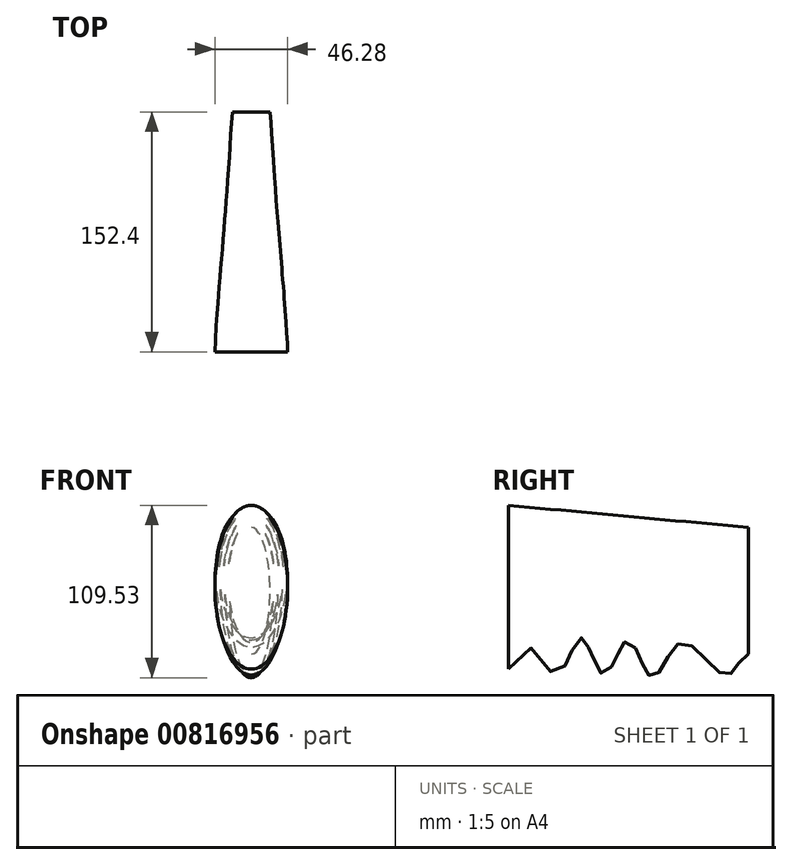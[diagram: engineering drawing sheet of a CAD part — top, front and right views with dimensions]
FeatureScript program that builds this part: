
annotation { "Feature Type Name" : "Feature", "Feature Type Description" : "" }
export const myFeature = defineFeature(function(context is Context, id is Id, definition is map)
    precondition{}
    {
        {
            var Q0;
            Q0=qCreatedBy(makeId("Front.planeOp"),FACE);
            var sketch = newSketch(context, id + "F0", { "sketchPlane" : qUnion([Q0])});
            skEllipse(sketch, "E0", {"center": v(0, -2.3) * mm, "majorRadius": 40.19 * mm, "minorRadius": 11.9 * mm, "majorAxis": v(0, 1)});
            skPoint(sketch, "E1", {"position": v(0, 37.89) * mm});
            skPoint(sketch, "E2", {"position": v(0, -42.49) * mm});
            skSolve(sketch);
        }
        {
            var Q0;
            Q0=qCreatedBy(makeId("Front.planeOp"),FACE);
            cPlane(context, id + "F1", {"entities" : qUnion([Q0]), "cplaneType" : CPlaneType.OFFSET, "offset" : 152.4 * mm, "width" : 152.4 * mm, "height" : 152.4 * mm});
        }
        {
            var Q0;
            Q0=qCreatedBy(id+"F1.planeOp",FACE);
            var sketch = newSketch(context, id + "F2", { "sketchPlane" : qUnion([Q0])});
            skEllipse(sketch, "E3", {"center": v(0, 0) * mm, "majorRadius": 52.02 * mm, "minorRadius": 23.14 * mm, "majorAxis": v(0, 1)});
            skPoint(sketch, "E4", {"position": v(0, 52.02) * mm});
            skPoint(sketch, "E5", {"position": v(0, -52.02) * mm});
            skSolve(sketch);
        }
        {
            var Q0;
            Q0=qCreatedBy(makeId("Right.planeOp"),FACE);
            var sketch = newSketch(context, id + "F3", { "sketchPlane" : qUnion([Q0])});
            skFitSpline(sketch, "E6", {"points": [v(-152.4, 52.02) * mm, v(0, 37.89) * mm], "startDerivative": vector(152.54, -14.57) * mm, "endDerivative": vector(152.54, -14.57) * mm});
            skFitSpline(sketch, "E7", {"points": [v(-152.4, -52.02) * mm, v(-123.4, -55.65) * mm, v(-106.61, -32.12) * mm, v(-92.02, -55.47) * mm, v(-76.51, -33.58) * mm, v(-61.2, -57.48) * mm, v(-42.57, -35.19) * mm, v(-13.95, -56.2) * mm, v(0, -42.49) * mm], "startDerivative": vector(311.42, 755.49) * mm, "endDerivative": vector(151.88, 8.9) * mm});
            skSolve(sketch);
        }
        {
            var Q0;
            Q0=makeQuery(id+"F2.imprint","IMPRINT",FACE,{"disambiguationData":[TD([[makeQuery(id+"F2.imprint","IMPRINT",EDGE,{"derivedFrom":sQuery(id+"F2.wireOp",EDGE,"E3")}),1.0]])]});
            var Q1;
            Q1=makeQuery(id+"F0.imprint","IMPRINT",FACE,{"disambiguationData":[TD([[makeQuery(id+"F0.imprint","IMPRINT",EDGE,{"derivedFrom":sQuery(id+"F0.wireOp",EDGE,"E0")}),1.0]])]});
            var Q2;
            Q2=sQuery(id+"F3.wireOp",EDGE,"E6");
            var Q3;
            Q3=sQuery(id+"F3.wireOp",EDGE,"E7");
            loft(context, id + "F4", {"addGuides" : true, "sheetProfilesArray" : [{ "sheetProfileEntities" : qUnion([Q0]) }, { "sheetProfileEntities" : qUnion([Q1]) }], "guidesArray" : [{ "guideEntities" : qUnion([Q2]), "guideDerivativeType" : LoftGuideDerivativeType.DEFAULT, "guideDerivativeMagnitude" : 1 }, { "guideEntities" : qUnion([Q3]), "guideDerivativeType" : LoftGuideDerivativeType.DEFAULT, "guideDerivativeMagnitude" : 1 }]});
        }
    });
